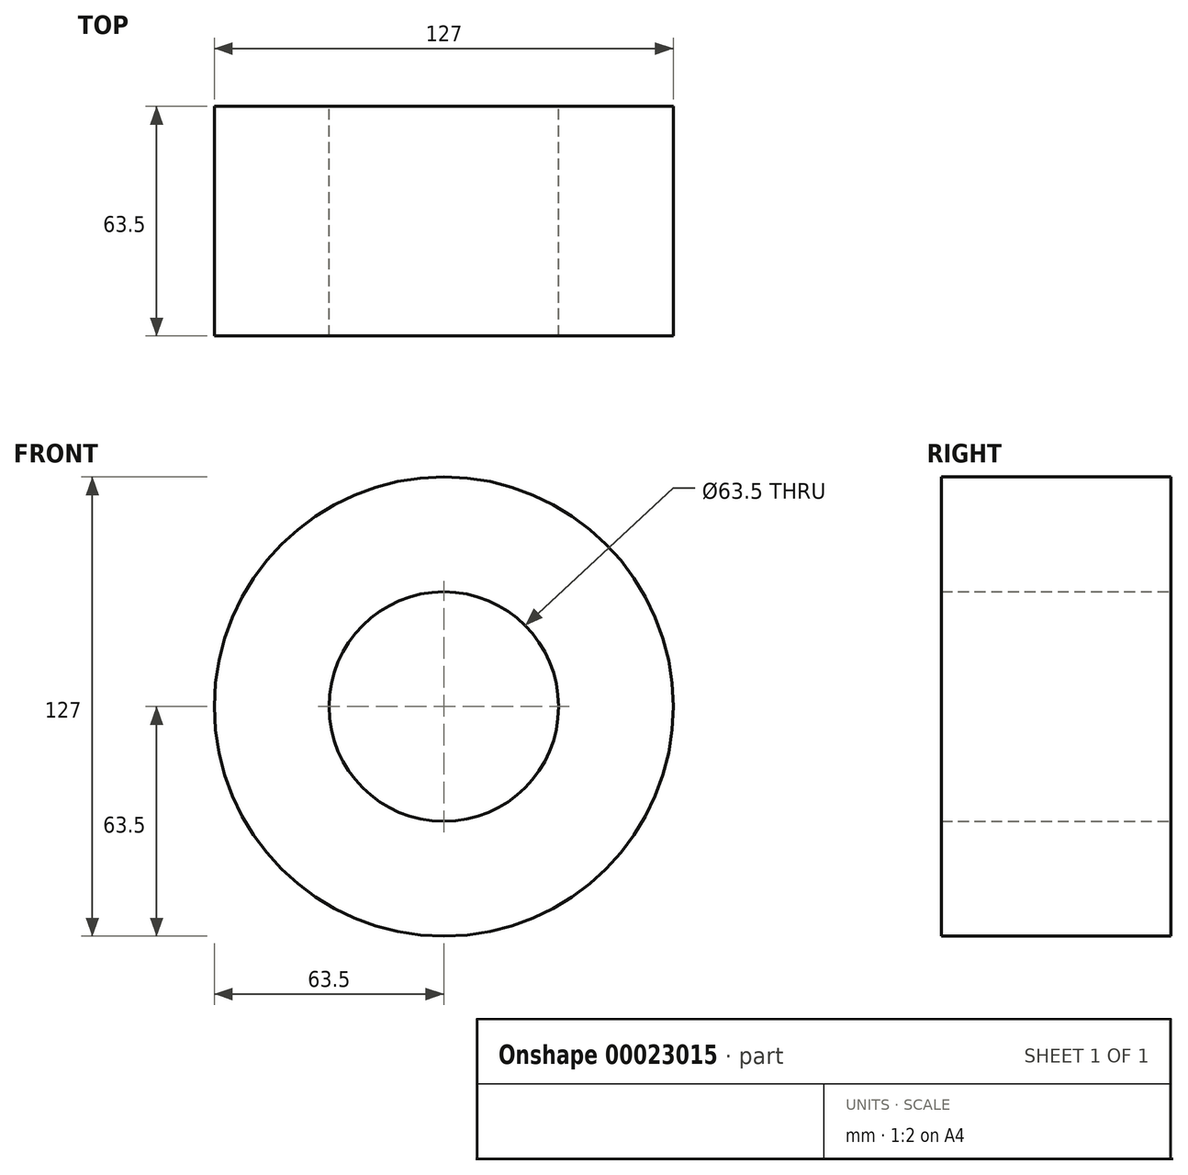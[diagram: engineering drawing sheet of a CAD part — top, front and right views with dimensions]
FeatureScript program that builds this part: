
annotation { "Feature Type Name" : "Feature", "Feature Type Description" : "" }
export const myFeature = defineFeature(function(context is Context, id is Id, definition is map)
    precondition{}
    {
        {
            var Q0;
            Q0=qCreatedBy(makeId("Front.planeOp"),FACE);
            var sketch = newSketch(context, id + "F0", { "sketchPlane" : qUnion([Q0])});
            skCircle(sketch, "E0", {"center": v(0, 0) * mm, "radius": 63.5 * mm});
            skCircle(sketch, "E1", {"center": v(0, 0) * mm, "radius": 31.75 * mm});
            skSolve(sketch);
        }
        {
            var Q0;
            Q0=makeQuery(id+"F0.imprint","IMPRINT",FACE,{"disambiguationData":[TD([[makeQuery(id+"F0.imprint","IMPRINT",EDGE,{"derivedFrom":sQuery(id+"F0.wireOp",EDGE,"E0")}),1.0]])]});
            var Q1;
            Q1=sQuery(id+"F0.wireOp",EDGE,"E0");
            extrude(context, id + "F1", {"entities" : qUnion([Q0]), "surfaceEntities" : qUnion([Q1]), "depth" : 63.5 * mm});
        }
    });
